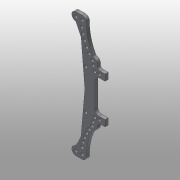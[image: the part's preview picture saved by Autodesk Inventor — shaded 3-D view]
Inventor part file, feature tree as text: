
AUTODESK INVENTOR PART (.ipt)
format: ipt  version: 2016 (Build 200138000, 138)  size: 200,704 bytes
history: native  units: mm
features: extrude x1, mirror x1, sketch x1
ambient origin geometry x8: Origin, YZ Plane, XZ Plane, XY Plane, X Axis, Y Axis, Z Axis, Center Point
bodies: Body1 (feature_tree)
feature tree (3):
  extrude  "Extrusion2"  TaperAngle=0.0deg  [1 undecoded]
  mirror  "Mirror1"
  sketch  "Sketch1"  dims[d0=28.0mm d1=0.0mm d2=2.0mm d3=4.0mm d4=12.0mm d5=0.0mm d6=10.0mm d8=0.872665mm d9=3.490659mm d10=4.0mm d11=4.0mm d12=50.0mm d13=4.0mm d14=3.0mm d15=54.0mm d16=1.797689mm d17=4.625123mm d18=27.35mm d19=12.4mm d20=3.0mm d21=56.0mm d22=0.0mm d23=60.0mm d25=4.625123mm d28=3.0mm d29=3.0mm d30=3.0mm d31=5.5mm d32=4.5mm d34=19.0mm d35=3.0mm d36=4.5mm d38=13.0mm d39=3.0mm d40=6.0mm d42=3.0mm d43=3.0mm d44=2.0mm d47=3.0mm d48=0.0mm]
note: 1 required parameter value undecoded (feature->parameter linkage not recoverable at this tier; creation-order binding heuristic only, values carry confidence <= 0.55)
